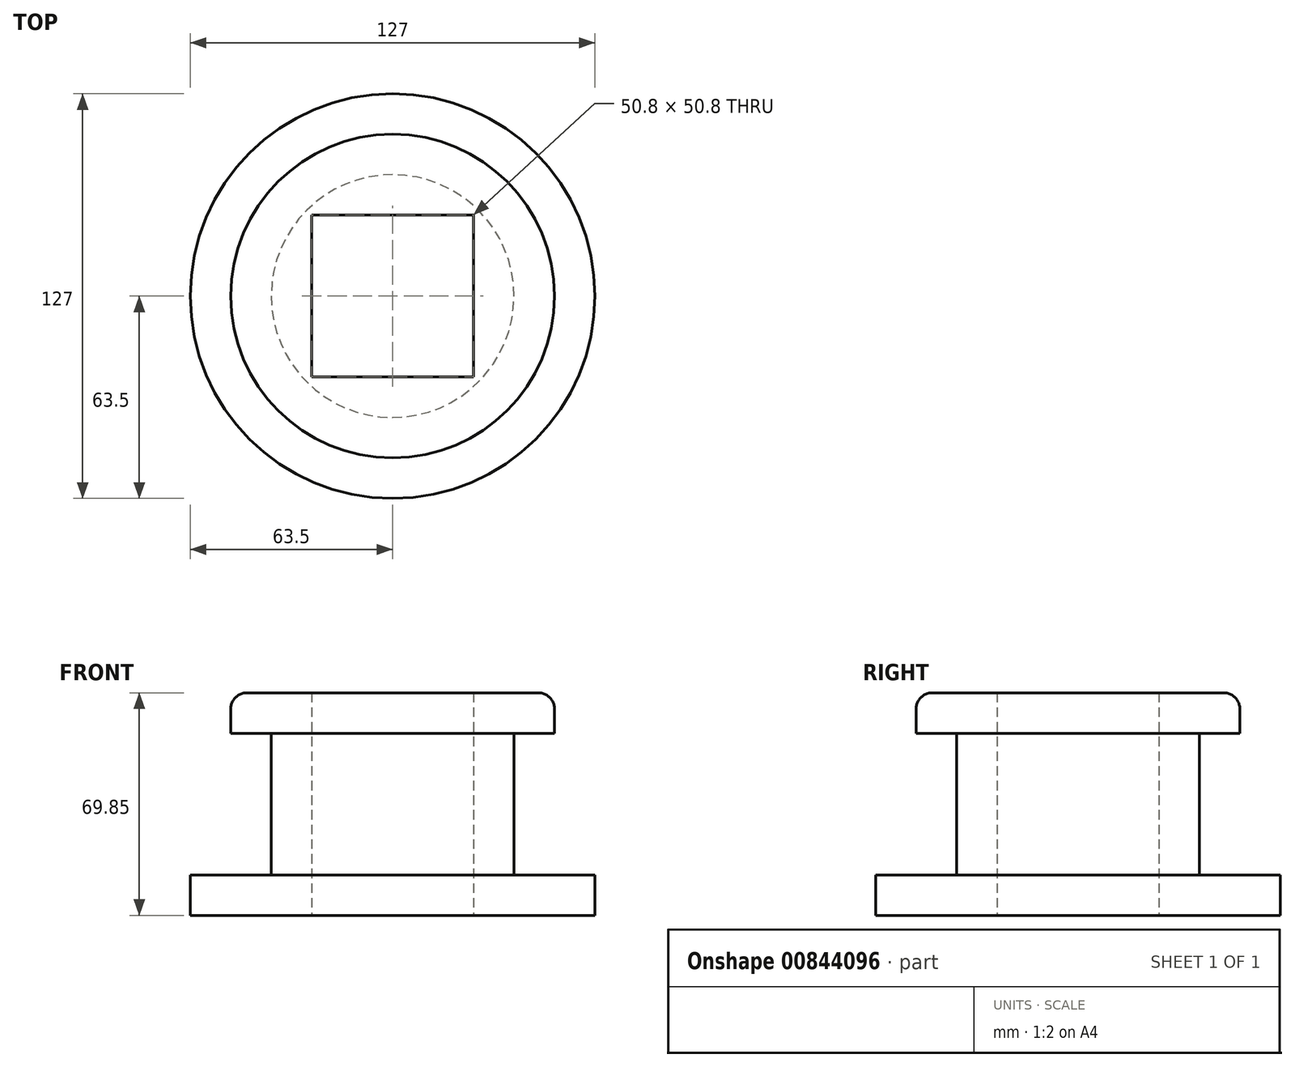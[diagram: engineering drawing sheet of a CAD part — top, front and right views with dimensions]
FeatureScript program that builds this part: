
annotation { "Feature Type Name" : "Feature", "Feature Type Description" : "" }
export const myFeature = defineFeature(function(context is Context, id is Id, definition is map)
    precondition{}
    {
        {
            var Q0;
            Q0=qCreatedBy(makeId("Top.planeOp"),FACE);
            var sketch = newSketch(context, id + "F0", { "sketchPlane" : qUnion([Q0])});
            skCircle(sketch, "E0", {"center": v(0, 0) * mm, "radius": 63.5 * mm});
            skSolve(sketch);
        }
        {
            var Q0;
            Q0 = qSketchRegion(id + "F0", true);
            extrude(context, id + "F1", {"entities" : qUnion([Q0]), "depth" : 12.7 * mm, "offsetDistance" : 25.4 * mm});
        }
        {
            var Q0;
            Q0=qCreatedBy(makeId("Top.planeOp"),FACE);
            var sketch = newSketch(context, id + "F2", { "sketchPlane" : qUnion([Q0])});
            skCircle(sketch, "E1", {"center": v(0, 0) * mm, "radius": 38.1 * mm});
            skSolve(sketch);
        }
        {
            var Q0;
            Q0 = qSketchRegion(id + "F2", true);
            extrude(context, id + "F3", {"entities" : qUnion([Q0]), "operationType" : NewBodyOperationType.ADD, "depth" : 57.15 * mm, "offsetDistance" : 25.4 * mm});
        }
        {
            var Q0;
            Q0=makeQuery(id+"F3.opExtrude","CAP_FACE",FACE,{"disambiguationData":[OSD([sQuery(id+"F2.wireOp",EDGE,"E1")])],"isStart":false});
            var sketch = newSketch(context, id + "F4", { "sketchPlane" : qUnion([Q0])});
            skCircle(sketch, "E2", {"center": v(0, 0) * mm, "radius": 50.8 * mm});
            skSolve(sketch);
        }
        {
            var Q0;
            Q0 = qSketchRegion(id + "F4", true);
            extrude(context, id + "F5", {"entities" : qUnion([Q0]), "operationType" : NewBodyOperationType.ADD, "depth" : 12.7 * mm, "offsetDistance" : 25.4 * mm});
        }
        {
            var Q0;
            Q0=qCreatedBy(makeId("Top.planeOp"),FACE);
            var sketch = newSketch(context, id + "F6", { "sketchPlane" : qUnion([Q0])});
            skLineSegment(sketch, "E3.bottom", {"start": v(25.4, -25.4) * mm, "end": v(-25.4, -25.4) * mm});
            skLineSegment(sketch, "E3.top", {"start": v(25.4, 25.4) * mm, "end": v(-25.4, 25.4) * mm});
            skLineSegment(sketch, "E3.left", {"start": v(25.4, -25.4) * mm, "end": v(25.4, 25.4) * mm});
            skLineSegment(sketch, "E3.right", {"start": v(-25.4, -25.4) * mm, "end": v(-25.4, 25.4) * mm});
            skPoint(sketch, "E3.middle", {"position": v(0, 0) * mm});
            skSolve(sketch);
        }
        {
            var Q0;
            Q0=makeQuery(id+"F6.imprint","IMPRINT",FACE,{"disambiguationData":[TD([[makeQuery(id+"F6.imprint","IMPRINT",EDGE,{"derivedFrom":sQuery(id+"F6.wireOp",EDGE,"E3.bottom")}),-1.0]])]});
            extrude(context, id + "F7", {"entities" : qUnion([Q0]), "operationType" : NewBodyOperationType.REMOVE, "depth" : 82.55 * mm, "offsetDistance" : 25.4 * mm});
        }
        {
            var Q0;
            Q0=qCreatedBy(makeId("Top.planeOp"),FACE);
            var sketch = newSketch(context, id + "F8", { "sketchPlane" : qUnion([Q0])});
            skCircle(sketch, "E4", {"center": v(-50.8, 0) * mm, "radius": 6.35 * mm});
            skCircle(sketch, "E5", {"center": v(0, -50.8) * mm, "radius": 6.35 * mm});
            skCircle(sketch, "E6.MirrorC", {"center": v(0, 50.8) * mm, "radius": 6.35 * mm});
            skCircle(sketch, "E7.MirrorC", {"center": v(50.8, 0) * mm, "radius": 6.35 * mm});
            skSolve(sketch);
        }
        {
            var Q0;
            Q0 = qSketchRegion(id + "F8", true);
            extrude(context, id + "F9", {"entities" : qUnion([Q0]), "operationType" : NewBodyOperationType.REMOVE, "oppositeDirection" : true, "depth" : 12.7 * mm, "offsetDistance" : 25.4 * mm});
        }
        {
            var Q0;
            Q0=makeQuery(id+"F5.opExtrude","CAP_EDGE",EDGE,{"disambiguationData":[OSD([sQuery(id+"F4.wireOp",EDGE,"E2")])],"isStart":false});
            fillet(context, id + "F10", {"entities" : qUnion([Q0]), "radius" : 5.08 * mm, "tangentPropagation" : true, "allowEdgeOverflow" : false});
        }
    });
